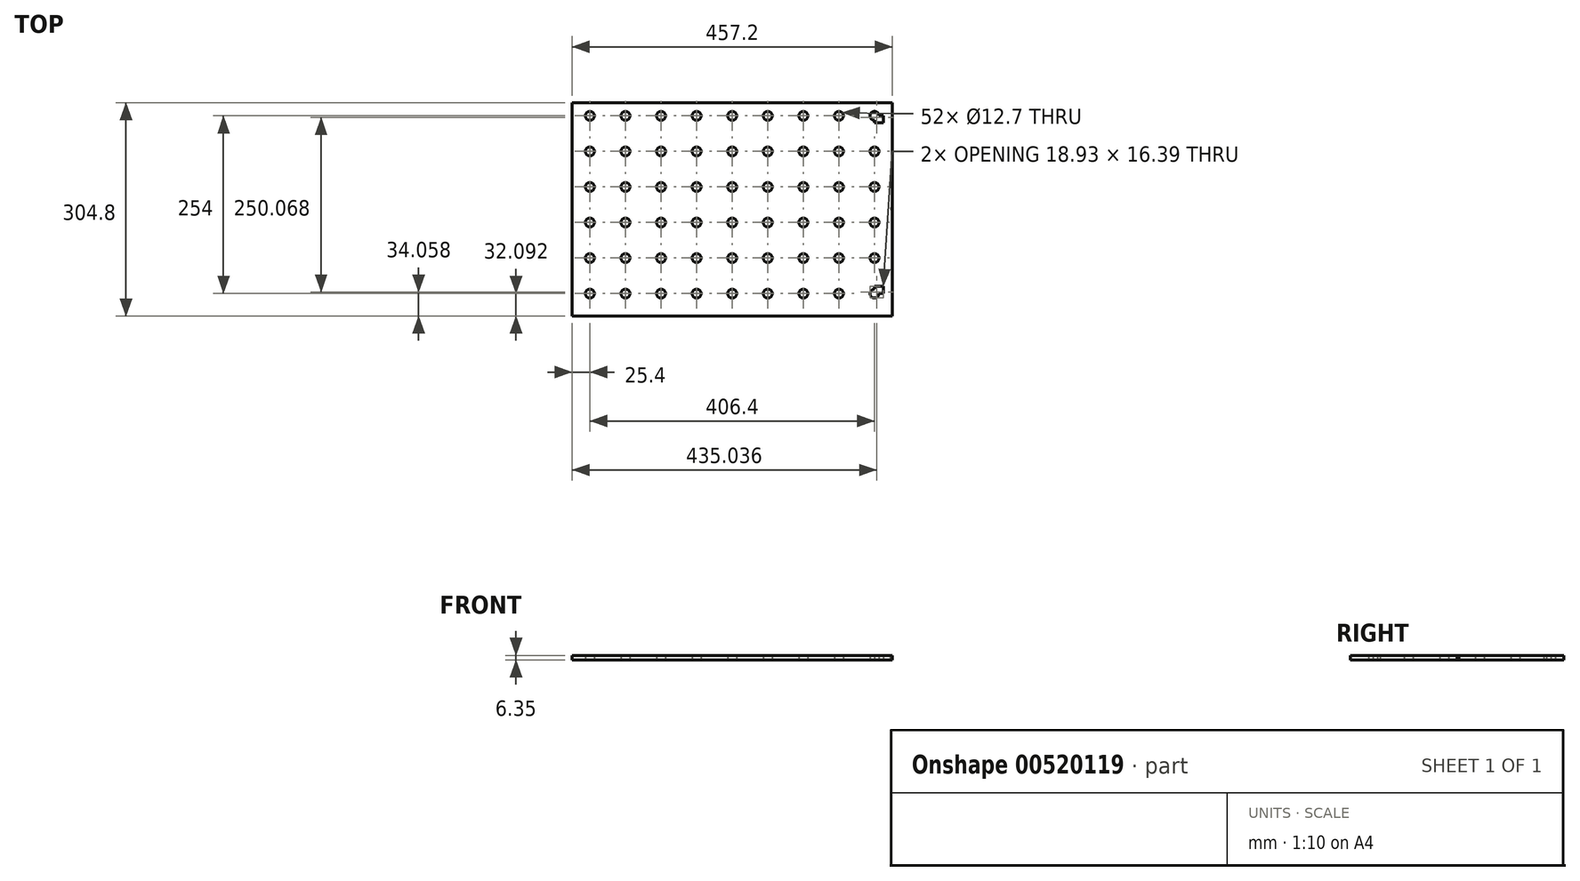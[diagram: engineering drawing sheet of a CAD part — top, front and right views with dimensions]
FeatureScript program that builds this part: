
annotation { "Feature Type Name" : "Feature", "Feature Type Description" : "" }
export const myFeature = defineFeature(function(context is Context, id is Id, definition is map)
    precondition{}
    {
        {
            var Q0;
            Q0=qCreatedBy(makeId("Top.planeOp"),FACE);
            var sketch = newSketch(context, id + "F0", { "sketchPlane" : qUnion([Q0])});
            skLineSegment(sketch, "E0.bottom", {"start": v(0, 0) * mm, "end": v(457.2, 0) * mm});
            skLineSegment(sketch, "E0.top", {"start": v(0, -304.8) * mm, "end": v(457.2, -304.8) * mm});
            skLineSegment(sketch, "E0.left", {"start": v(0, 0) * mm, "end": v(0, -304.8) * mm});
            skLineSegment(sketch, "E0.right", {"start": v(457.2, 0) * mm, "end": v(457.2, -304.8) * mm});
            skCircle(sketch, "E1", {"center": v(25.4, -272.7) * mm, "radius": 6.35 * mm});
            skCircle(sketch, "E2.0.1.0", {"center": v(25.4, -221.9) * mm, "radius": 6.35 * mm});
            skCircle(sketch, "E2.0.2.0", {"center": v(25.4, -171.1) * mm, "radius": 6.35 * mm});
            skCircle(sketch, "E2.0.3.0", {"center": v(25.4, -120.3) * mm, "radius": 6.35 * mm});
            skCircle(sketch, "E2.0.4.0", {"center": v(25.4, -69.5) * mm, "radius": 6.35 * mm});
            skCircle(sketch, "E2.0.5.0", {"center": v(25.4, -18.7) * mm, "radius": 6.35 * mm});
            skCircle(sketch, "E2.1.0.0", {"center": v(76.2, -272.7) * mm, "radius": 6.35 * mm});
            skCircle(sketch, "E2.1.1.0", {"center": v(76.2, -221.9) * mm, "radius": 6.35 * mm});
            skCircle(sketch, "E2.1.2.0", {"center": v(76.2, -171.1) * mm, "radius": 6.35 * mm});
            skCircle(sketch, "E2.1.3.0", {"center": v(76.2, -120.3) * mm, "radius": 6.35 * mm});
            skCircle(sketch, "E2.1.4.0", {"center": v(76.2, -69.5) * mm, "radius": 6.35 * mm});
            skCircle(sketch, "E2.1.5.0", {"center": v(76.2, -18.7) * mm, "radius": 6.35 * mm});
            skCircle(sketch, "E2.2.0.0", {"center": v(127, -272.7) * mm, "radius": 6.35 * mm});
            skCircle(sketch, "E2.2.1.0", {"center": v(127, -221.9) * mm, "radius": 6.35 * mm});
            skCircle(sketch, "E2.2.2.0", {"center": v(127, -171.1) * mm, "radius": 6.35 * mm});
            skCircle(sketch, "E2.2.3.0", {"center": v(127, -120.3) * mm, "radius": 6.35 * mm});
            skCircle(sketch, "E2.2.4.0", {"center": v(127, -69.5) * mm, "radius": 6.35 * mm});
            skCircle(sketch, "E2.2.5.0", {"center": v(127, -18.7) * mm, "radius": 6.35 * mm});
            skCircle(sketch, "E2.3.0.0", {"center": v(177.8, -272.7) * mm, "radius": 6.35 * mm});
            skCircle(sketch, "E2.3.1.0", {"center": v(177.8, -221.9) * mm, "radius": 6.35 * mm});
            skCircle(sketch, "E2.3.2.0", {"center": v(177.8, -171.1) * mm, "radius": 6.35 * mm});
            skCircle(sketch, "E2.3.3.0", {"center": v(177.8, -120.3) * mm, "radius": 6.35 * mm});
            skCircle(sketch, "E2.3.4.0", {"center": v(177.8, -69.5) * mm, "radius": 6.35 * mm});
            skCircle(sketch, "E2.3.5.0", {"center": v(177.8, -18.7) * mm, "radius": 6.35 * mm});
            skCircle(sketch, "E2.4.0.0", {"center": v(228.6, -272.7) * mm, "radius": 6.35 * mm});
            skCircle(sketch, "E2.4.1.0", {"center": v(228.6, -221.9) * mm, "radius": 6.35 * mm});
            skCircle(sketch, "E2.4.2.0", {"center": v(228.6, -171.1) * mm, "radius": 6.35 * mm});
            skCircle(sketch, "E2.4.3.0", {"center": v(228.6, -120.3) * mm, "radius": 6.35 * mm});
            skCircle(sketch, "E2.4.4.0", {"center": v(228.6, -69.5) * mm, "radius": 6.35 * mm});
            skCircle(sketch, "E2.4.5.0", {"center": v(228.6, -18.7) * mm, "radius": 6.35 * mm});
            skCircle(sketch, "E2.5.0.0", {"center": v(279.4, -272.7) * mm, "radius": 6.35 * mm});
            skCircle(sketch, "E2.5.1.0", {"center": v(279.4, -221.9) * mm, "radius": 6.35 * mm});
            skCircle(sketch, "E2.5.2.0", {"center": v(279.4, -171.1) * mm, "radius": 6.35 * mm});
            skCircle(sketch, "E2.5.3.0", {"center": v(279.4, -120.3) * mm, "radius": 6.35 * mm});
            skCircle(sketch, "E2.5.4.0", {"center": v(279.4, -69.5) * mm, "radius": 6.35 * mm});
            skCircle(sketch, "E2.5.5.0", {"center": v(279.4, -18.7) * mm, "radius": 6.35 * mm});
            skCircle(sketch, "E2.6.0.0", {"center": v(330.2, -272.7) * mm, "radius": 6.35 * mm});
            skCircle(sketch, "E2.6.1.0", {"center": v(330.2, -221.9) * mm, "radius": 6.35 * mm});
            skCircle(sketch, "E2.6.2.0", {"center": v(330.2, -171.1) * mm, "radius": 6.35 * mm});
            skCircle(sketch, "E2.6.3.0", {"center": v(330.2, -120.3) * mm, "radius": 6.35 * mm});
            skCircle(sketch, "E2.6.4.0", {"center": v(330.2, -69.5) * mm, "radius": 6.35 * mm});
            skCircle(sketch, "E2.6.5.0", {"center": v(330.2, -18.7) * mm, "radius": 6.35 * mm});
            skCircle(sketch, "E2.7.0.0", {"center": v(381, -272.7) * mm, "radius": 6.35 * mm});
            skCircle(sketch, "E2.7.1.0", {"center": v(381, -221.9) * mm, "radius": 6.35 * mm});
            skCircle(sketch, "E2.7.2.0", {"center": v(381, -171.1) * mm, "radius": 6.35 * mm});
            skCircle(sketch, "E2.7.3.0", {"center": v(381, -120.3) * mm, "radius": 6.35 * mm});
            skCircle(sketch, "E2.7.4.0", {"center": v(381, -69.5) * mm, "radius": 6.35 * mm});
            skCircle(sketch, "E2.7.5.0", {"center": v(381, -18.7) * mm, "radius": 6.35 * mm});
            skArc(sketch, "E2.8.0.0", {"start": v(431.8, -266.36) * mm, "mid": v(427.3, -277.2) * mm, "end": v(438.15, -272.7) * mm});
            skCircle(sketch, "E2.8.1.0", {"center": v(431.8, -221.9) * mm, "radius": 6.35 * mm});
            skCircle(sketch, "E2.8.2.0", {"center": v(431.8, -171.1) * mm, "radius": 6.35 * mm});
            skCircle(sketch, "E2.8.3.0", {"center": v(431.8, -120.3) * mm, "radius": 6.35 * mm});
            skCircle(sketch, "E2.8.4.0", {"center": v(431.8, -69.5) * mm, "radius": 6.35 * mm});
            skArc(sketch, "E2.8.5.0", {"start": v(438.15, -18.7) * mm, "mid": v(427.3, -14.22) * mm, "end": v(431.8, -25.06) * mm});
            skLineSegment(sketch, "E2.direction1", {"start": v(25.4, -272.7) * mm, "end": v(76.2, -272.7) * mm, "construction": true});
            skLineSegment(sketch, "E2.direction2", {"start": v(25.4, -272.7) * mm, "end": v(25.4, -221.9) * mm, "construction": true});
            skLineSegment(sketch, "E3", {"start": v(438.15, -18.7) * mm, "end": v(444.5, -18.7) * mm});
            skLineSegment(sketch, "E4", {"start": v(444.5, -18.7) * mm, "end": v(444.5, -28.87) * mm});
            skLineSegment(sketch, "E5", {"start": v(444.5, -28.87) * mm, "end": v(431.8, -28.87) * mm});
            skLineSegment(sketch, "E6", {"start": v(431.8, -28.87) * mm, "end": v(431.8, -25.06) * mm});
            skLineSegment(sketch, "E7", {"start": v(438.15, -272.7) * mm, "end": v(444.5, -272.7) * mm});
            skLineSegment(sketch, "E8", {"start": v(444.5, -272.7) * mm, "end": v(444.5, -262.55) * mm});
            skLineSegment(sketch, "E9", {"start": v(444.5, -262.55) * mm, "end": v(431.8, -262.55) * mm});
            skLineSegment(sketch, "E10", {"start": v(431.8, -262.55) * mm, "end": v(431.8, -266.36) * mm});
            skSolve(sketch);
        }
        {
            var Q0;
            Q0=makeQuery(id+"F0.imprint","IMPRINT",FACE,{"disambiguationData":[TD([[makeQuery(id+"F0.imprint","IMPRINT",EDGE,{"derivedFrom":sQuery(id+"F0.wireOp",EDGE,"E0.bottom")}),-1.0]])]});
            extrude(context, id + "F1", {"entities" : qUnion([Q0]), "depth" : 6.35 * mm, "offsetDistance" : 25.4 * mm});
        }
        {
            var Q0;
            Q0=makeQuery(id+"F1.opExtrude","SWEPT_FACE",FACE,{"disambiguationData":[OSD([sQuery(id+"F0.wireOp",EDGE,"E0.right")])]});
            var sketch = newSketch(context, id + "F2", { "sketchPlane" : qUnion([Q0])});
            skLineSegment(sketch, "E11", {"start": v(-152.4, 0) * mm, "end": v(-152.4, 5.08) * mm});
            skLineSegment(sketch, "E12", {"start": v(-152.4, 5.08) * mm, "end": v(-149.86, 5.08) * mm});
            skLineSegment(sketch, "E13", {"start": v(-149.86, 5.08) * mm, "end": v(-149.86, 0) * mm});
            skLineSegment(sketch, "E14", {"start": v(-149.86, 0) * mm, "end": v(-152.4, 0) * mm});
            skSolve(sketch);
        }
        {
            var Q0;
            Q0 = qSketchRegion(id + "F2", true);
            extrude(context, id + "F3", {"entities" : qUnion([Q0]), "operationType" : NewBodyOperationType.REMOVE, "oppositeDirection" : true, "depth" : 2.54 * mm, "offsetDistance" : 25.4 * mm});
        }
    });
